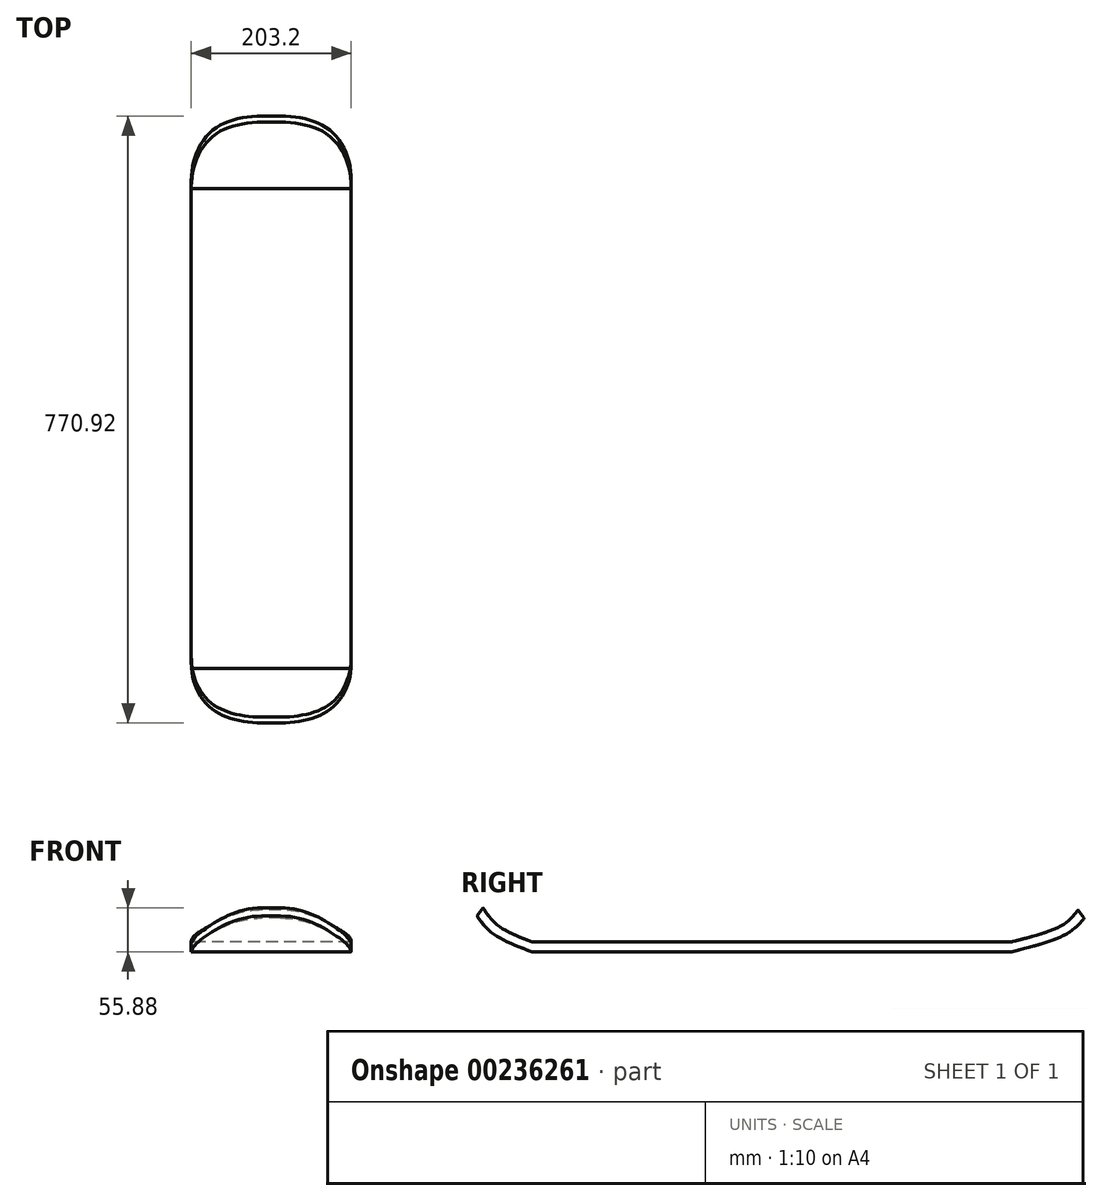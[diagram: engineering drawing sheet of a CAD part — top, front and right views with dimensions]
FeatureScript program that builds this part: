
annotation { "Feature Type Name" : "Feature", "Feature Type Description" : "" }
export const myFeature = defineFeature(function(context is Context, id is Id, definition is map)
    precondition{}
    {
        {
            var Q0;
            Q0=qCreatedBy(makeId("Top.planeOp"),FACE);
            var sketch = newSketch(context, id + "F0", { "sketchPlane" : qUnion([Q0])});
            skLineSegment(sketch, "E0.bottom", {"start": v(101.6, 304.8) * mm, "end": v(-101.6, 304.8) * mm});
            skLineSegment(sketch, "E0.top", {"start": v(101.6, -304.8) * mm, "end": v(-101.6, -304.8) * mm});
            skLineSegment(sketch, "E0.left", {"start": v(101.6, 304.8) * mm, "end": v(101.6, -304.8) * mm});
            skLineSegment(sketch, "E0.right", {"start": v(-101.6, 304.8) * mm, "end": v(-101.6, -304.8) * mm});
            skPoint(sketch, "E0.middle", {"position": v(0, 0) * mm});
            skSolve(sketch);
        }
        {
            var Q0;
            Q0 = qSketchRegion(id + "F0", true);
            extrude(context, id + "F1", {"entities" : qUnion([Q0]), "endBound" : BoundingType.SYMMETRIC, "depth" : 12.7 * mm});
        }
        {
            var Q0;
            Q0=qCreatedBy(makeId("Right.planeOp"),FACE);
            var sketch = newSketch(context, id + "F2", { "sketchPlane" : qUnion([Q0])});
            skFitSpline(sketch, "E1", {"points": [v(306.4, 0) * mm, v(373.38, 22.52) * mm, v(394.12, 42.67) * mm], "startDerivative": vector(127.1, 32.44) * mm, "endDerivative": vector(42.12, 54.52) * mm});
            skSolve(sketch);
        }
        {
            var Q0;
            Q0=makeQuery(id+"F1.opExtrude","SWEPT_FACE",FACE,{"disambiguationData":[OSD([sQuery(id+"F0.wireOp",EDGE,"E0.bottom")])]});
            var Q1;
            Q1=sQuery(id+"F2.wireOp",EDGE,"E1");
            sweep(context, id + "F3", {"operationType" : NewBodyOperationType.ADD, "profiles" : qUnion([Q0]), "path" : qUnion([Q1])});
        }
        {
            var Q0;
            Q0=qCreatedBy(makeId("Right.planeOp"),FACE);
            var sketch = newSketch(context, id + "F4", { "sketchPlane" : qUnion([Q0])});
            skFitSpline(sketch, "E2", {"points": [v(-305.97, 0) * mm, v(-352.35, 22.5) * mm, v(-371.45, 45.02) * mm], "startDerivative": vector(-92.05, 35.92) * mm, "endDerivative": vector(-36.34, 55) * mm});
            skSolve(sketch);
        }
        {
            var Q0;
            Q0=makeQuery(id+"F1.opExtrude","SWEPT_FACE",FACE,{"disambiguationData":[OSD([sQuery(id+"F0.wireOp",EDGE,"E0.top")])]});
            var Q1;
            Q1=sQuery(id+"F4.wireOp",EDGE,"E2");
            sweep(context, id + "F5", {"operationType" : NewBodyOperationType.ADD, "profiles" : qUnion([Q0]), "path" : qUnion([Q1])});
        }
        {
            var Q0;
            Q0=makeQuery(id+"F5.opSweep","CAP_EDGE",EDGE,{"disambiguationData":[OSD([sQuery(id+"F0.wireOp",EDGE,"E0.top"),sQuery(id+"F0.wireOp",EDGE,"E0.right"),sQuery(id+"F4.wireOp",VERTEX,"E2.end")])],"isStart":false});
            var Q1;
            Q1=makeQuery(id+"F5.opSweep","CAP_EDGE",EDGE,{"disambiguationData":[OSD([sQuery(id+"F0.wireOp",EDGE,"E0.top"),sQuery(id+"F0.wireOp",EDGE,"E0.left"),sQuery(id+"F4.wireOp",VERTEX,"E2.end")])],"isStart":false});
            var Q2;
            Q2=makeQuery(id+"F3.opSweep","CAP_EDGE",EDGE,{"disambiguationData":[OSD([sQuery(id+"F0.wireOp",EDGE,"E0.bottom"),sQuery(id+"F0.wireOp",EDGE,"E0.left"),sQuery(id+"F2.wireOp",VERTEX,"E1.end")])],"isStart":false});
            var Q3;
            Q3=makeQuery(id+"F3.opSweep","CAP_EDGE",EDGE,{"disambiguationData":[OSD([sQuery(id+"F0.wireOp",EDGE,"E0.bottom"),sQuery(id+"F0.wireOp",EDGE,"E0.right"),sQuery(id+"F2.wireOp",VERTEX,"E1.end")])],"isStart":false});
            fillet(context, id + "F6", {"entities" : qUnion([Q0, Q1, Q2, Q3]), "radius" : 89.53 * mm, "tangentPropagation" : true, "allowEdgeOverflow" : false});
        }
    });
